# Revit family: Haworth_Intuity_Benching_Return
name_source: partatom
category: Furniture Systems
revit_build: Autodesk Revit 2018 (Build: 20170223_1515(x64)
units: mm (PartAtom-declared; Revit-internal decimal feet)

## family parameters
Always vertical = Yes
Cut with Voids When Loaded = No
OmniClass Number = 23.40.70.14.64.21
OmniClass Title = Systems Furniture
Part Type = Normal
Room Calculation Point = No
Round Connector Dimension = Use Diameter
Shared = No
Work Plane-Based = No

## types (6) — shared parameters
Access Plate Finish = Haworth _ Paint _ Metallic Silver
Actual Height = 29 3/16"
Assembly Code = E2020200
Back Leg Offset = 1"
Custom Size = No
Description = Haworth - Intuity - Benching Return
Leg Finish = Haworth _ Paint _ Metallic Silver
Leg Half = 1"
Leg Height = 28"
Leg Offset = 1 1/4"
Manufacturer = Haworth
Max Width = 60"
Min Width = 48"
Model = Haworth - Intuity - Benching Return
Revision Number = 2
Size = Verify Final Dim. w/ Haworth
Standard Return Widths = 48, 54, 60 inches
Sustainability Info = https://www.haworth.com
Top Thickness = 1 3/16"
URL = https://www.haworth.com
URL - Product = http://www.haworth.com
Warranty = http://www.haworth.com
Worksurface Finish = Haworth _ Laminate _ Linen H-WL

## per-type parameters (varying)
| type | 24 Depth | 30 Depth | Actual Width | Actual Worksurface Depth | Width |
| 24d 48w | Yes | No | 48" | 24" | 48" |
| 24d 54w | Yes | No | 54" | 24" | 54" |
| 24d 60w | Yes | No | 60" | 24" | 60" |
| 30d 48w | No | Yes | 48" | 30" | 48" |
| 30d 54w | No | Yes | 54" | 30" | 54" |
| 30d 60w | No | Yes | 60" | 30" | 60" |

## geometry (parser evidence)
native form markers: Sweep x17
no freeform markers — native parametric forms only
